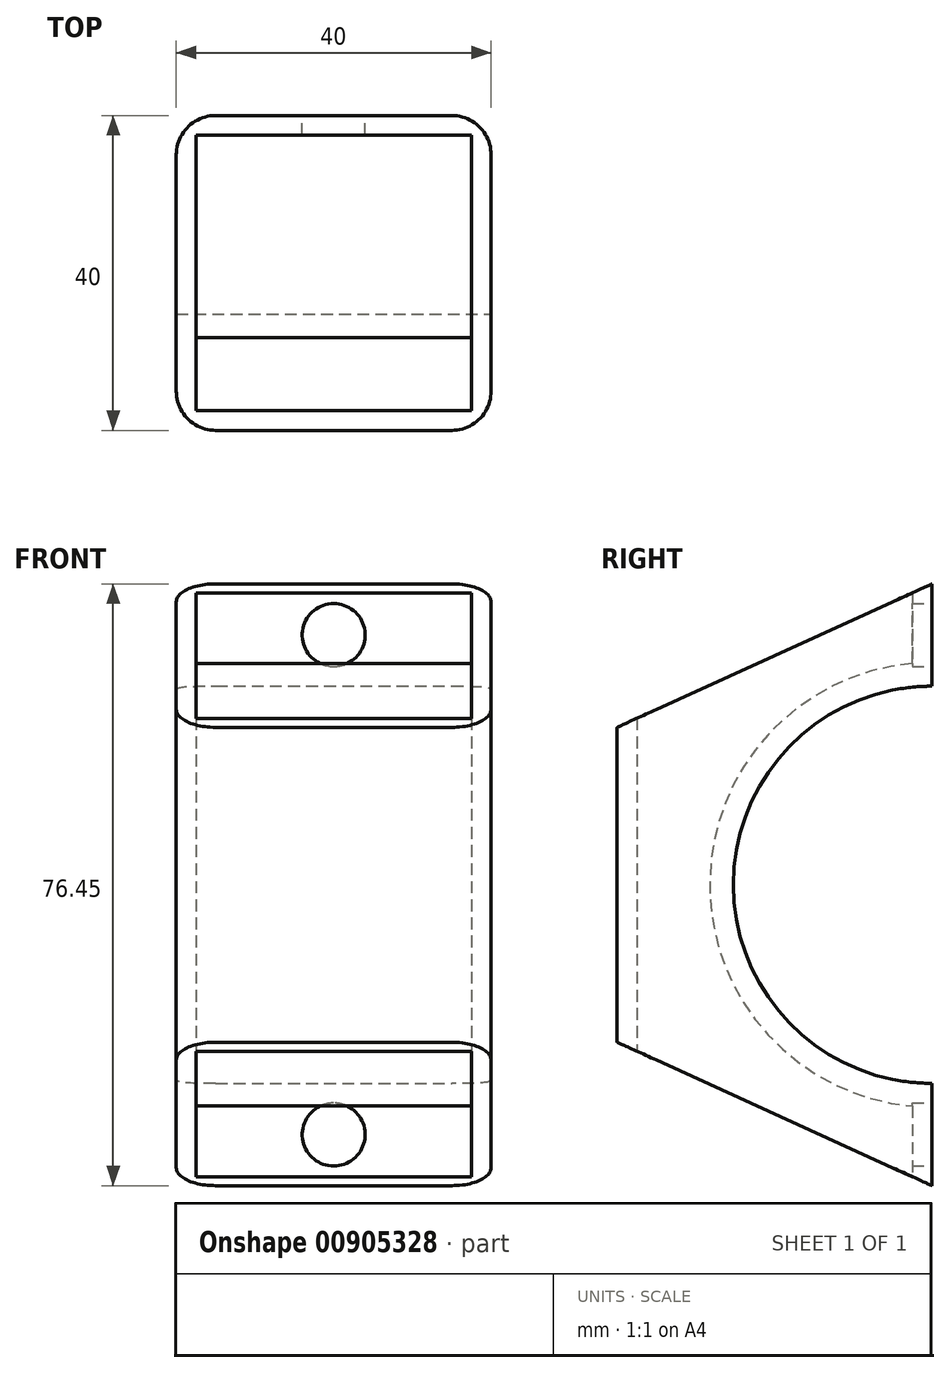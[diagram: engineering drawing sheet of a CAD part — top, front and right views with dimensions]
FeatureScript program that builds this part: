
annotation { "Feature Type Name" : "Feature", "Feature Type Description" : "" }
export const myFeature = defineFeature(function(context is Context, id is Id, definition is map)
    precondition{}
    {
        {
            var Q0;
            Q0=qCreatedBy(makeId("Top.planeOp"),FACE);
            var sketch = newSketch(context, id + "F0", { "sketchPlane" : qUnion([Q0])});
            skLineSegment(sketch, "E0.bottom", {"start": v(-20, 20) * mm, "end": v(20, 20) * mm});
            skLineSegment(sketch, "E0.top", {"start": v(-20, -20) * mm, "end": v(20, -20) * mm});
            skLineSegment(sketch, "E0.left", {"start": v(-20, 20) * mm, "end": v(-20, -20) * mm});
            skLineSegment(sketch, "E0.right", {"start": v(20, 20) * mm, "end": v(20, -20) * mm});
            skLineSegment(sketch, "E1.bottom", {"start": v(-17.5, 17.5) * mm, "end": v(17.5, 17.5) * mm});
            skLineSegment(sketch, "E1.top", {"start": v(-17.5, -17.5) * mm, "end": v(17.5, -17.5) * mm});
            skLineSegment(sketch, "E1.left", {"start": v(-17.5, 17.5) * mm, "end": v(-17.5, -17.5) * mm});
            skLineSegment(sketch, "E1.right", {"start": v(17.5, 17.5) * mm, "end": v(17.5, -17.5) * mm});
            skSolve(sketch);
        }
        {
            var Q0;
            Q0=qSketchRegion(id+"F0",true);
            extrude(context, id + "F1", {"entities" : qUnion([Q0]), "depth" : 100 * mm, "offsetDistance" : 25 * mm});
        }
        {
            var Q0;
            Q0=makeQuery(id+"F1.opExtrude","SWEPT_FACE",FACE,{"disambiguationData":[OSD([sQuery(id+"F0.wireOp",EDGE,"E0.right")])]});
            var sketch = newSketch(context, id + "F2", { "sketchPlane" : qUnion([Q0])});
            skArc(sketch, "E2", {"start": v(20, 75.8) * mm, "mid": v(-5.23, 50.57) * mm, "end": v(20, 25.34) * mm});
            skArc(sketch, "E3", {"start": v(20, 78.8) * mm, "mid": v(-8.23, 50.57) * mm, "end": v(20, 22.34) * mm});
            skLineSegment(sketch, "E4", {"start": v(20, 78.8) * mm, "end": v(20, 22.34) * mm});
            skLineSegment(sketch, "E5", {"start": v(-20, 70.57) * mm, "end": v(-20, 30.57) * mm});
            skLineSegment(sketch, "E6", {"start": v(20, 22.34) * mm, "end": v(20, 12.34) * mm});
            skLineSegment(sketch, "E7", {"start": v(20, 12.34) * mm, "end": v(-20, 30.57) * mm});
            skLineSegment(sketch, "E8", {"start": v(20, 78.8) * mm, "end": v(20, 88.8) * mm});
            skLineSegment(sketch, "E9", {"start": v(20, 88.8) * mm, "end": v(-20, 70.57) * mm});
            skSolve(sketch);
        }
        {
            var Q0;
            {var subQ0=sQuery(id+"F2.wireOp",EDGE,"E2");Q0=makeQuery(id+"F2.imprint","IMPRINT",FACE,{"disambiguationData":[TD([[makeQuery(id+"F2.imprint","IMPRINT",EDGE,{"derivedFrom":subQ0}),1.0]])]});}
            var Q1;
            {var subQ0=sQuery(id+"F2.wireOp",EDGE,"E2");Q1=makeQuery(id+"F2.imprint","IMPRINT",FACE,{"disambiguationData":[TD([[makeQuery(id+"F2.imprint","IMPRINT",EDGE,{"derivedFrom":subQ0}),-1.0]])]});}
            var Q2;
            {var subQ0=sQuery(id+"F2.wireOp",EDGE,"E7");Q2=makeQuery(id+"F2.imprint","IMPRINT",FACE,{"disambiguationData":[TD([[makeQuery(id+"F2.imprint","IMPRINT",EDGE,{"derivedFrom":subQ0}),1.0]])]});}
            var Q3;
            {var subQ0=sQuery(id+"F2.wireOp",EDGE,"E9");Q3=makeQuery(id+"F2.imprint","IMPRINT",FACE,{"disambiguationData":[TD([[makeQuery(id+"F2.imprint","IMPRINT",EDGE,{"derivedFrom":subQ0}),-1.0]])]});}
            extrude(context, id + "F3", {"entities" : qUnion([Q0, Q1, Q2, Q3]), "operationType" : NewBodyOperationType.REMOVE, "endBound" : BoundingType.THROUGH_ALL, "oppositeDirection" : true, "depth" : 25 * mm, "offsetDistance" : 25 * mm});
        }
        {
            var Q0;
            {var subQ0=sQuery(id+"F2.wireOp",EDGE,"E2");Q0=makeQuery(id+"F2.imprint","IMPRINT",FACE,{"disambiguationData":[TD([[makeQuery(id+"F2.imprint","IMPRINT",EDGE,{"derivedFrom":subQ0}),-1.0]])]});}
            extrude(context, id + "F4", {"entities" : qUnion([Q0]), "operationType" : NewBodyOperationType.ADD, "oppositeDirection" : true, "depth" : 40 * mm, "offsetDistance" : 25 * mm});
        }
        {
            var Q0;
            {var subQ0=sQuery(id+"F2.wireOp",EDGE,"E4");Q0=makeQuery(id+"F4.boolean.opBoolean","MERGE",FACE,{"derivedFrom":[makeQuery(id+"F3.boolean.opBoolean","SPLIT",FACE,{"disambiguationData":[TD([makeQuery(id+"F3.opExtrude","SWEPT_FACE",FACE,{"disambiguationData":[OSD([sQuery(id+"F2.wireOp",EDGE,"E9")])]})])],"derivedFrom":makeQuery(id+"F1.opExtrude","SWEPT_FACE",FACE,{"disambiguationData":[OSD([sQuery(id+"F0.wireOp",EDGE,"E0.bottom")])]})}),makeQuery(id+"F4.opExtrude","SWEPT_FACE",FACE,{"disambiguationData":[OSD([subQ0]),TDD([makeQuery(id+"F2.imprint","IMPRINT",EDGE,{"disambiguationData":[TD([[makeQuery(id+"F2.imprint","INTERSECT",VERTEX,{"disambiguationData":[OD(0.0)],"derivedFrom":[sQuery(id+"F2.wireOp",EDGE,"E2"),subQ0]}),1.0]])],"derivedFrom":subQ0})])]})]});}
            var sketch = newSketch(context, id + "F5", { "sketchPlane" : qUnion([Q0])});
            skCircle(sketch, "E10", {"center": v(0, 82.3) * mm, "radius": 4 * mm});
            skSolve(sketch);
        }
        {
            var Q0;
            Q0=qSketchRegion(id+"F5",true);
            extrude(context, id + "F6", {"entities" : qUnion([Q0]), "operationType" : NewBodyOperationType.REMOVE, "oppositeDirection" : true, "depth" : 2.5 * mm, "offsetDistance" : 25 * mm});
        }
        {
            var Q0;
            {var subQ0=sQuery(id+"F2.wireOp",EDGE,"E4");Q0=makeQuery(id+"F4.boolean.opBoolean","MERGE",FACE,{"derivedFrom":[makeQuery(id+"F3.boolean.opBoolean","SPLIT",FACE,{"disambiguationData":[TD([makeQuery(id+"F3.opExtrude","SWEPT_FACE",FACE,{"disambiguationData":[OSD([sQuery(id+"F2.wireOp",EDGE,"E7")])]})])],"derivedFrom":makeQuery(id+"F1.opExtrude","SWEPT_FACE",FACE,{"disambiguationData":[OSD([sQuery(id+"F0.wireOp",EDGE,"E0.bottom")])]})}),makeQuery(id+"F4.opExtrude","SWEPT_FACE",FACE,{"disambiguationData":[OSD([subQ0]),TDD([makeQuery(id+"F2.imprint","IMPRINT",EDGE,{"disambiguationData":[TD([[makeQuery(id+"F2.imprint","INTERSECT",VERTEX,{"disambiguationData":[OD(1.0)],"derivedFrom":[sQuery(id+"F2.wireOp",EDGE,"E2"),subQ0]}),-1.0]])],"derivedFrom":subQ0})])]})]});}
            var sketch = newSketch(context, id + "F7", { "sketchPlane" : qUnion([Q0])});
            skLineSegment(sketch, "E11", {"start": v(0, 12.34) * mm, "end": v(0, 25.34) * mm});
            skCircle(sketch, "E12", {"center": v(0, 18.84) * mm, "radius": 4 * mm});
            skSolve(sketch);
        }
        {
            var Q0;
            Q0=qSketchRegion(id+"F7",true);
            extrude(context, id + "F8", {"entities" : qUnion([Q0]), "operationType" : NewBodyOperationType.REMOVE, "oppositeDirection" : true, "depth" : 2.5 * mm, "offsetDistance" : 25 * mm});
        }
        {
            var Q0;
            {var subQ0=sQuery(id+"F2.wireOp",EDGE,"E4");var subQ2=sQuery(id+"F0.wireOp",EDGE,"E0.bottom");var subQ3=sQuery(id+"F0.wireOp",EDGE,"E0.left");Q0=makeQuery(id+"F4.boolean.opBoolean","MERGE",EDGE,{"derivedFrom":[makeQuery(id+"F3.boolean.opBoolean","SPLIT",EDGE,{"disambiguationData":[TD([makeQuery(id+"F3.opExtrude","SWEPT_FACE",FACE,{"disambiguationData":[OSD([sQuery(id+"F2.wireOp",EDGE,"E9")])]})])],"derivedFrom":makeQuery(id+"F1.opExtrude","SWEPT_EDGE",EDGE,{"disambiguationData":[OSD([subQ2,subQ3])]})}),makeQuery(id+"F4.opExtrude","CAP_EDGE",EDGE,{"disambiguationData":[OSD([subQ0]),TDD([makeQuery(id+"F2.imprint","IMPRINT",EDGE,{"disambiguationData":[TD([[makeQuery(id+"F2.imprint","INTERSECT",VERTEX,{"disambiguationData":[OD(0.0)],"derivedFrom":[sQuery(id+"F2.wireOp",EDGE,"E2"),subQ0]}),1.0]])],"derivedFrom":subQ0})])],"isStart":false})]});}
            var Q1;
            {var subQ0=sQuery(id+"F2.wireOp",EDGE,"E4");var subQ2=sQuery(id+"F0.wireOp",EDGE,"E0.bottom");var subQ3=sQuery(id+"F0.wireOp",EDGE,"E0.left");Q1=makeQuery(id+"F4.boolean.opBoolean","MERGE",EDGE,{"derivedFrom":[makeQuery(id+"F3.boolean.opBoolean","SPLIT",EDGE,{"disambiguationData":[TD([makeQuery(id+"F3.opExtrude","SWEPT_FACE",FACE,{"disambiguationData":[OSD([sQuery(id+"F2.wireOp",EDGE,"E7")])]})])],"derivedFrom":makeQuery(id+"F1.opExtrude","SWEPT_EDGE",EDGE,{"disambiguationData":[OSD([subQ2,subQ3])]})}),makeQuery(id+"F4.opExtrude","CAP_EDGE",EDGE,{"disambiguationData":[OSD([subQ0]),TDD([makeQuery(id+"F2.imprint","IMPRINT",EDGE,{"disambiguationData":[TD([[makeQuery(id+"F2.imprint","INTERSECT",VERTEX,{"disambiguationData":[OD(1.0)],"derivedFrom":[sQuery(id+"F2.wireOp",EDGE,"E2"),subQ0]}),-1.0]])],"derivedFrom":subQ0})])],"isStart":false})]});}
            var Q2;
            Q2=makeQuery(id+"F1.opExtrude","SWEPT_EDGE",EDGE,{"disambiguationData":[OSD([sQuery(id+"F0.wireOp",EDGE,"E0.top"),sQuery(id+"F0.wireOp",EDGE,"E0.left")])]});
            var Q3;
            Q3=makeQuery(id+"F1.opExtrude","SWEPT_EDGE",EDGE,{"disambiguationData":[OSD([sQuery(id+"F0.wireOp",EDGE,"E0.top"),sQuery(id+"F0.wireOp",EDGE,"E0.right")])]});
            var Q4;
            {var subQ0=sQuery(id+"F2.wireOp",EDGE,"E4");var subQ2=sQuery(id+"F0.wireOp",EDGE,"E0.bottom");var subQ3=sQuery(id+"F0.wireOp",EDGE,"E0.right");Q4=makeQuery(id+"F4.boolean.opBoolean","MERGE",EDGE,{"derivedFrom":[makeQuery(id+"F3.boolean.opBoolean","SPLIT",EDGE,{"disambiguationData":[TD([makeQuery(id+"F3.opExtrude","SWEPT_FACE",FACE,{"disambiguationData":[OSD([sQuery(id+"F2.wireOp",EDGE,"E7")])]})])],"derivedFrom":makeQuery(id+"F1.opExtrude","SWEPT_EDGE",EDGE,{"disambiguationData":[OSD([subQ2,subQ3])]})}),makeQuery(id+"F4.opExtrude","CAP_EDGE",EDGE,{"disambiguationData":[OSD([subQ0]),TDD([makeQuery(id+"F2.imprint","IMPRINT",EDGE,{"disambiguationData":[TD([[makeQuery(id+"F2.imprint","INTERSECT",VERTEX,{"disambiguationData":[OD(1.0)],"derivedFrom":[sQuery(id+"F2.wireOp",EDGE,"E2"),subQ0]}),-1.0]])],"derivedFrom":subQ0})])],"isStart":true})]});}
            var Q5;
            {var subQ0=sQuery(id+"F2.wireOp",EDGE,"E4");var subQ2=sQuery(id+"F0.wireOp",EDGE,"E0.bottom");var subQ3=sQuery(id+"F0.wireOp",EDGE,"E0.right");Q5=makeQuery(id+"F4.boolean.opBoolean","MERGE",EDGE,{"derivedFrom":[makeQuery(id+"F3.boolean.opBoolean","SPLIT",EDGE,{"disambiguationData":[TD([makeQuery(id+"F3.opExtrude","SWEPT_FACE",FACE,{"disambiguationData":[OSD([sQuery(id+"F2.wireOp",EDGE,"E9")])]})])],"derivedFrom":makeQuery(id+"F1.opExtrude","SWEPT_EDGE",EDGE,{"disambiguationData":[OSD([subQ2,subQ3])]})}),makeQuery(id+"F4.opExtrude","CAP_EDGE",EDGE,{"disambiguationData":[OSD([subQ0]),TDD([makeQuery(id+"F2.imprint","IMPRINT",EDGE,{"disambiguationData":[TD([[makeQuery(id+"F2.imprint","INTERSECT",VERTEX,{"disambiguationData":[OD(0.0)],"derivedFrom":[sQuery(id+"F2.wireOp",EDGE,"E2"),subQ0]}),1.0]])],"derivedFrom":subQ0})])],"isStart":true})]});}
            fillet(context, id + "F9", {"entities" : qUnion([Q0, Q1, Q2, Q3, Q4, Q5]), "radius" : 5 * mm, "tangentPropagation" : true, "allowEdgeOverflow" : false});
        }
    });
